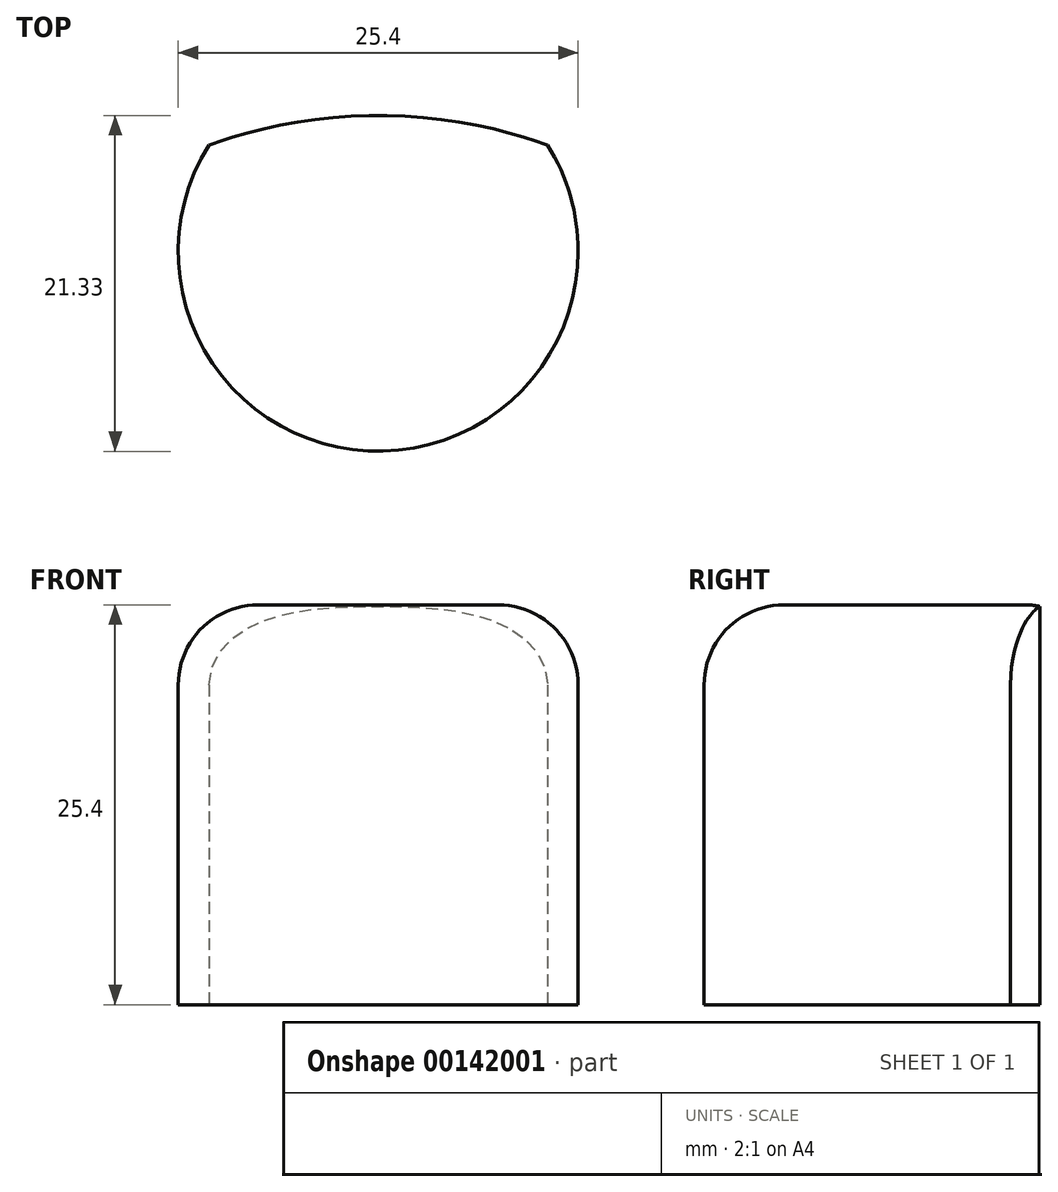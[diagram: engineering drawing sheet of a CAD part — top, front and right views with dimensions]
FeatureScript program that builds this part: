
annotation { "Feature Type Name" : "Feature", "Feature Type Description" : "" }
export const myFeature = defineFeature(function(context is Context, id is Id, definition is map)
    precondition{}
    {
        {
            var Q0;
            Q0=qCreatedBy(makeId("Top.planeOp"),FACE);
            var sketch = newSketch(context, id + "F0", { "sketchPlane" : qUnion([Q0])});
            skCircle(sketch, "E0", {"center": v(0, 0) * mm, "radius": 63.5 * mm});
            skCircle(sketch, "E1", {"center": v(0, 0) * mm, "radius": 12.7 * mm});
            skCircle(sketch, "E2", {"center": v(0, -23.12) * mm, "radius": 31.75 * mm});
            skSolve(sketch);
        }
        {
            var Q0;
            {var subQ0=sQuery(id+"F0.wireOp",EDGE,"E2");var subQ1=sQuery(id+"F0.wireOp",EDGE,"E1");var subQ2=makeQuery(id+"F0.imprint","INTERSECT",VERTEX,{"disambiguationData":[OD(0.0)],"derivedFrom":[subQ1,subQ0]});Q0=makeQuery(id+"F0.imprint","IMPRINT",FACE,{"disambiguationData":[TD([[makeQuery(id+"F0.imprint","IMPRINT",EDGE,{"disambiguationData":[TD([[subQ2,-1.0]])],"derivedFrom":subQ1}),1.0]])]});}
            extrude(context, id + "F1", {"entities" : qUnion([Q0]), "depth" : 25.4 * mm});
        }
        {
            var Q0;
            Q0=makeQuery(id+"F1.opExtrude","CAP_EDGE",EDGE,{"disambiguationData":[OSD([sQuery(id+"F0.wireOp",EDGE,"E1")])],"isStart":false});
            fillet(context, id + "F2", {"entities" : qUnion([Q0]), "radius" : 5.08 * mm, "tangentPropagation" : true, "allowEdgeOverflow" : false});
        }
    });
